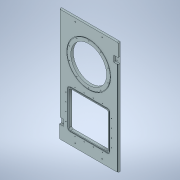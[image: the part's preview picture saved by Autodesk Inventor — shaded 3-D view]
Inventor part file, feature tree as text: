
AUTODESK INVENTOR PART (.ipt)
format: ipt  version: 2021 (Build 250183000, 183)  size: 221,696 bytes
history: imported  units: in
note: dims shown in document units (in); Inventor stores cm internally (conversion verified against a paired STEP export)
features: imported_body x1
ambient origin geometry x8: Origin, YZ Plane, XZ Plane, XY Plane, X Axis, Y Axis, Z Axis, Center Point
bodies: Solid1 (imported_parasolid), Body1 (imported_parasolid)
feature tree (1):
  imported_body  NMx_Import_Brep_tag  [imported B-rep: ~163 faces, bbox_mm=[360.0, 690.0, 15.875]]
